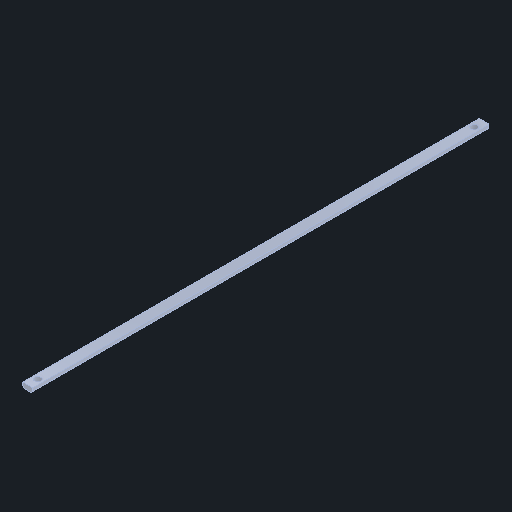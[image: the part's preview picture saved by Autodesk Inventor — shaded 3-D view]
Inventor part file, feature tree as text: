
AUTODESK INVENTOR PART (.ipt)
format: ipt  version: 2025 (Build 290162000, 162)  size: 171,520 bytes
history: native  units: in
note: dims shown in document units (in); Inventor stores cm internally (conversion verified against a paired STEP export)
features: extrude x4, sketch x4, thicken_offset x1, other x1
ambient origin geometry x8: Origin, YZ Plane, XZ Plane, XY Plane, X Axis, Y Axis, Z Axis, Center Point
bodies: Solid1 (feature_tree)
feature tree (10):
  extrude  "Extrusion1"  Depth=12.1875in
  thicken_offset  "Thicken1"
  extrude  "Extrusion2"  Depth=12.625in
  extrude  "Extrusion3"  Depth=0.165in
  extrude  "Extrusion4"  Depth=0.125in
  sketch  "Sketch2"  dims[d0=0.0625in d1=0.0in d2=12.1875in]
  sketch  "Sketch3"  dims[d3=12.125in d4=12.625in]
  sketch  "Sketch4"  dims[d5=0.0in d6=0.165in]
  sketch  "Sketch5"  dims[d7=0.165in d8=11.0in d9=0.25in d10=11.0in d11=0.0in d12=0.125in d13=0.0in]
  other  "Cut-Revolve3"
